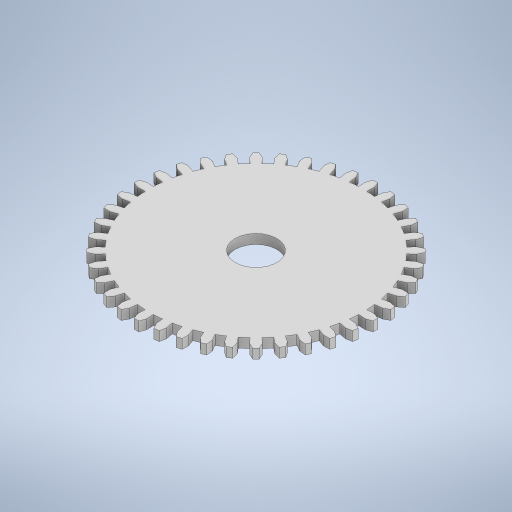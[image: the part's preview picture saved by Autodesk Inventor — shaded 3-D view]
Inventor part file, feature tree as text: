
AUTODESK INVENTOR PART (.ipt)
format: ipt  version: 2024.1 (Build 281209000, 209)  size: 563,200 bytes
history: native  units: mm
features: other x1, extrude x1, sketch x1
ambient origin geometry x8: Origin, YZ Plane, XZ Plane, XY Plane, X Axis, Y Axis, Z Axis, Center Point
bodies: Body1 (feature_tree)
feature tree (3):
  other  "ソリッド1"
  extrude  "押し出し1"  Depth=120.0mm
  sketch  "スケッチ1"
